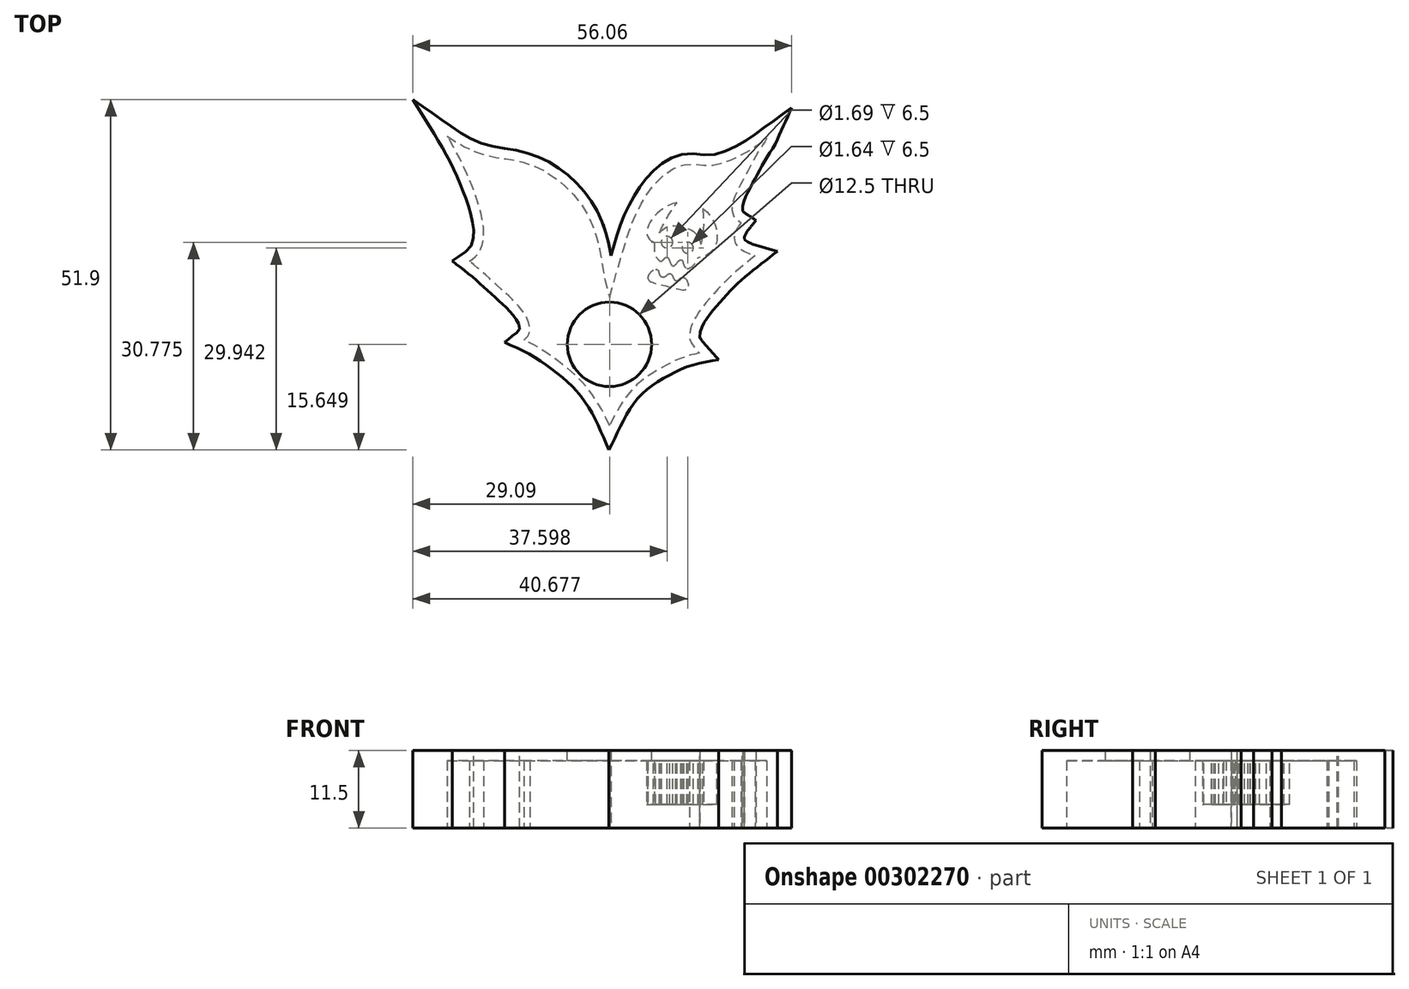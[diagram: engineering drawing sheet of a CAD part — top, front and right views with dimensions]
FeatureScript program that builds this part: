
annotation { "Feature Type Name" : "Feature", "Feature Type Description" : "" }
export const myFeature = defineFeature(function(context is Context, id is Id, definition is map)
    precondition{}
    {
        {
            var Q0;
            Q0=qCreatedBy(makeId("Top.planeOp"),FACE);
            var sketch = newSketch(context, id + "F0", { "sketchPlane" : qUnion([Q0])});
            skFitSpline(sketch, "E0", {"points": [v(0, 0) * mm, v(1.04, 3.6) * mm, v(2.03, 6.95) * mm, v(3.25, 10.76) * mm, v(4.89, 14.16) * mm, v(6.76, 16.83) * mm, v(10, 19.35) * mm, v(12.88, 19.71) * mm, v(14.8, 19.52) * mm, v(16.93, 19.96) * mm, v(18.82, 20.76) * mm, v(20.5, 21.6) * mm, v(21.92, 22.52) * mm, v(23.27, 23.54) * mm], "startDerivative": vector(11.6, 40.55) * mm, "endDerivative": vector(24.76, 17.84) * mm});
            skFitSpline(sketch, "E1", {"points": [v(23.27, 23.54) * mm, v(22.1, 21.65) * mm, v(20.11, 18.01) * mm, v(18.73, 15.37) * mm, v(18.17, 13.5) * mm, v(18.38, 12.02) * mm, v(19.5, 11.05) * mm], "startDerivative": vector(-5, -10.96) * mm, "endDerivative": vector(10.3, -6.8) * mm});
            skFitSpline(sketch, "E2", {"points": [v(19.5, 11.05) * mm, v(18.76, 9.95) * mm, v(18.55, 8.2) * mm, v(19.7, 6.95) * mm, v(21, 6.33) * mm, v(21.59, 6.15) * mm], "startDerivative": vector(-3.95, -4.92) * mm, "endDerivative": vector(3.93, -1.1) * mm});
            skFitSpline(sketch, "E3", {"points": [v(21.59, 6.15) * mm, v(17.73, 2.92) * mm, v(14.4, -0.7) * mm, v(12.34, -3.74) * mm, v(11.84, -5.76) * mm, v(13.28, -8.26) * mm], "startDerivative": vector(-16.93, -13.28) * mm, "endDerivative": vector(21.99, -24.7) * mm});
            skFitSpline(sketch, "E4", {"points": [v(13.28, -8.26) * mm, v(10.25, -9.17) * mm, v(7.27, -10.7) * mm, v(4.45, -12.6) * mm, v(1.93, -15.5) * mm, v(0, -19.05) * mm], "startDerivative": vector(-16.4, -3.11) * mm, "endDerivative": vector(-8.4, -17.05) * mm});
            skLineSegment(sketch, "E5", {"start": v(0, -19.05) * mm, "end": v(0, 0) * mm});
            skFitSpline(sketch, "E6", {"points": [v(0, -19.05) * mm, v(-0.9, -17.11) * mm, v(-2.62, -14.33) * mm, v(-4.57, -12) * mm, v(-6.78, -10.1) * mm, v(-9.56, -8.07) * mm, v(-12.7, -6.32) * mm], "startDerivative": vector(-5.74, 13.22) * mm, "endDerivative": vector(-19.61, 8.86) * mm});
            skFitSpline(sketch, "E7", {"points": [v(-12.7, -6.32) * mm, v(-12.04, -5.63) * mm, v(-11.85, -4.07) * mm, v(-13.19, -1.63) * mm, v(-15.32, 0.55) * mm, v(-17.96, 2.95) * mm, v(-20.74, 5.32) * mm], "startDerivative": vector(7, 5.62) * mm, "endDerivative": vector(-14.7, 11.22) * mm});
            skFitSpline(sketch, "E8", {"points": [v(-20.74, 5.32) * mm, v(-19.71, 6.16) * mm, v(-18.83, 7.76) * mm, v(-18.68, 10.62) * mm, v(-19.75, 14.85) * mm, v(-21.16, 18.36) * mm, v(-22.38, 20.96) * mm, v(-24.02, 23.9) * mm], "startDerivative": vector(10.92, 7.52) * mm, "endDerivative": vector(-11.35, 18.47) * mm});
            skFitSpline(sketch, "E9", {"points": [v(-24.02, 23.9) * mm, v(-21.5, 22.3) * mm, v(-18.1, 21) * mm, v(-15.1, 20.46) * mm, v(-13, 20.04) * mm, v(-9.87, 18.82) * mm, v(-6.05, 15.96) * mm, v(-3.38, 12.49) * mm, v(-1.86, 8.75) * mm, v(-1.06, 4.82) * mm, v(-0.6, 2.23) * mm, v(0, 0) * mm], "startDerivative": vector(27.7, -19.41) * mm, "endDerivative": vector(8.6, -29.29) * mm});
            skSolve(sketch);
        }
        {
            var Q0;
            Q0 = qSketchRegion(id + "F0", true);
            extrude(context, id + "F1", {"entities" : qUnion([Q0]), "depth" : 10 * mm});
        }
        {
            var Q0;
            Q0=makeQuery(id+"F1.opExtrude","CAP_FACE",FACE,{"disambiguationData":[OSD([sQuery(id+"F0.wireOp",EDGE,"E0"),sQuery(id+"F0.wireOp",EDGE,"E1"),sQuery(id+"F0.wireOp",EDGE,"E2"),sQuery(id+"F0.wireOp",EDGE,"E3"),sQuery(id+"F0.wireOp",EDGE,"E4"),sQuery(id+"F0.wireOp",EDGE,"E6"),sQuery(id+"F0.wireOp",EDGE,"E7"),sQuery(id+"F0.wireOp",EDGE,"E8"),sQuery(id+"F0.wireOp",EDGE,"E9")])],"isStart":true});
            shell(context, id + "F2", {"entities" : qUnion([Q0]), "thickness" : 1.5 * mm, "oppositeDirection" : true});
        }
        {
            var Q0;
            Q0=makeQuery(id+"F1.opExtrude","CAP_FACE",FACE,{"disambiguationData":[OSD([sQuery(id+"F0.wireOp",EDGE,"E0"),sQuery(id+"F0.wireOp",EDGE,"E1"),sQuery(id+"F0.wireOp",EDGE,"E2"),sQuery(id+"F0.wireOp",EDGE,"E3"),sQuery(id+"F0.wireOp",EDGE,"E4"),sQuery(id+"F0.wireOp",EDGE,"E6"),sQuery(id+"F0.wireOp",EDGE,"E7"),sQuery(id+"F0.wireOp",EDGE,"E8"),sQuery(id+"F0.wireOp",EDGE,"E9")])],"isStart":false});
            var sketch = newSketch(context, id + "F3", { "sketchPlane" : qUnion([Q0])});
            skCircle(sketch, "E10", {"center": v(8.5, 8.16) * mm, "radius": 0.85 * mm});
            skCircle(sketch, "E11", {"center": v(11.59, 7.32) * mm, "radius": 0.82 * mm});
            skFitSpline(sketch, "E12", {"points": [v(7.37, 9.55) * mm, v(10.45, 10.48) * mm, v(13.48, 7.8) * mm], "startDerivative": vector(6.12, 7.14) * mm, "endDerivative": vector(1.27, -11.01) * mm});
            skFitSpline(sketch, "E13", {"points": [v(7.37, 9.55) * mm, v(9.98, 13.98) * mm], "startDerivative": vector(2.21, 4.52) * mm, "endDerivative": vector(3.42, 4.33) * mm});
            skFitSpline(sketch, "E14", {"points": [v(13.78, 13.16) * mm, v(13.48, 7.8) * mm], "startDerivative": vector(0.63, -5.05) * mm, "endDerivative": vector(-1.54, -5.1) * mm});
            skFitSpline(sketch, "E15", {"points": [v(13.78, 13.16) * mm, v(15.93, 8.86) * mm, v(13.14, 5.81) * mm], "startDerivative": vector(7.9, -5.3) * mm, "endDerivative": vector(-11.8, -2.2) * mm});
            skFitSpline(sketch, "E16", {"points": [v(9.98, 13.98) * mm, v(6.63, 11.99) * mm, v(6.54, 8.19) * mm], "startDerivative": vector(-3.92, -0.2) * mm, "endDerivative": vector(10.17, -4.16) * mm});
            skFitSpline(sketch, "E17", {"points": [v(6.54, 8.19) * mm, v(7.39, 5.43) * mm], "startDerivative": vector(0.96, -1.06) * mm, "endDerivative": vector(3.78, -3.06) * mm});
            skFitSpline(sketch, "E18", {"points": [v(7.39, 5.43) * mm, v(8.54, 5.91) * mm], "startDerivative": vector(1.52, -1.24) * mm, "endDerivative": vector(1.38, -0.47) * mm});
            skFitSpline(sketch, "E19", {"points": [v(8.54, 5.91) * mm, v(9.39, 4.63) * mm], "startDerivative": vector(1, 0) * mm, "endDerivative": vector(1.28, -0.38) * mm});
            skFitSpline(sketch, "E20", {"points": [v(9.39, 4.63) * mm, v(10.6, 5.55) * mm], "startDerivative": vector(1.06, -0.31) * mm, "endDerivative": vector(1, -0.3) * mm});
            skFitSpline(sketch, "E21", {"points": [v(10.6, 5.55) * mm, v(11.46, 4.24) * mm], "startDerivative": vector(1.03, 0.13) * mm, "endDerivative": vector(1.87, -0.7) * mm});
            skFitSpline(sketch, "E22", {"points": [v(11.46, 4.24) * mm, v(13.14, 5.81) * mm], "startDerivative": vector(1.5, -0.32) * mm, "endDerivative": vector(0.8, 2.16) * mm});
            skFitSpline(sketch, "E23", {"points": [v(5.71, 2.83) * mm, v(8.45, 1.66) * mm, v(11.53, 1.28) * mm], "startDerivative": vector(-0.49, -3.62) * mm, "endDerivative": vector(2.65, 2.57) * mm});
            skFitSpline(sketch, "E24", {"points": [v(5.71, 2.83) * mm, v(6.07, 3.66) * mm, v(6.84, 4.13) * mm], "startDerivative": vector(0.2, 1.79) * mm, "endDerivative": vector(1.53, 0.02) * mm});
            skFitSpline(sketch, "E25", {"points": [v(6.84, 4.13) * mm, v(7.3, 3.74) * mm, v(7.74, 3.03) * mm], "startDerivative": vector(2.21, -0.13) * mm, "endDerivative": vector(1.85, -0.55) * mm});
            skFitSpline(sketch, "E26", {"points": [v(7.74, 3.03) * mm, v(8.43, 3.2) * mm, v(8.91, 3.52) * mm], "startDerivative": vector(1.7, -0.42) * mm, "endDerivative": vector(1.37, -0.04) * mm});
            skFitSpline(sketch, "E27", {"points": [v(8.91, 3.52) * mm, v(9.4, 3.03) * mm, v(9.8, 2.48) * mm], "startDerivative": vector(1.45, -0.02) * mm, "endDerivative": vector(1.56, -0.4) * mm});
            skFitSpline(sketch, "E28", {"points": [v(9.8, 2.48) * mm, v(10.32, 2.65) * mm, v(11.01, 2.9) * mm], "startDerivative": vector(2.07, -0.5) * mm, "endDerivative": vector(2.08, -0.31) * mm});
            skFitSpline(sketch, "E29", {"points": [v(11.01, 2.9) * mm, v(11.6, 2.1) * mm, v(11.53, 1.28) * mm], "startDerivative": vector(1.82, -0.39) * mm, "endDerivative": vector(-1.23, -1.54) * mm});
            skSolve(sketch);
        }
        {
            var Q0;
            Q0=makeQuery(id+"F3.imprint","IMPRINT",FACE,{"disambiguationData":[TD([[makeQuery(id+"F3.imprint","IMPRINT",EDGE,{"derivedFrom":sQuery(id+"F3.wireOp",EDGE,"E10")}),-1.0]])]});
            var Q1;
            Q1=makeQuery(id+"F3.imprint","IMPRINT",FACE,{"disambiguationData":[TD([[makeQuery(id+"F3.imprint","IMPRINT",EDGE,{"derivedFrom":sQuery(id+"F3.wireOp",EDGE,"E23")}),1.0]])]});
            extrude(context, id + "F4", {"entities" : qUnion([Q0, Q1]), "operationType" : NewBodyOperationType.ADD, "oppositeDirection" : true, "depth" : 8 * mm, "offsetDistance" : 25 * mm});
        }
        {
            var Q0;
            Q0=makeQuery(id+"F1.opExtrude","CAP_FACE",FACE,{"disambiguationData":[OSD([sQuery(id+"F0.wireOp",EDGE,"E0"),sQuery(id+"F0.wireOp",EDGE,"E1"),sQuery(id+"F0.wireOp",EDGE,"E2"),sQuery(id+"F0.wireOp",EDGE,"E3"),sQuery(id+"F0.wireOp",EDGE,"E4"),sQuery(id+"F0.wireOp",EDGE,"E6"),sQuery(id+"F0.wireOp",EDGE,"E7"),sQuery(id+"F0.wireOp",EDGE,"E8"),sQuery(id+"F0.wireOp",EDGE,"E9")])],"isStart":false});
            var sketch = newSketch(context, id + "F5", { "sketchPlane" : qUnion([Q0])});
            skCircle(sketch, "E30", {"center": v(0, -6.97) * mm, "radius": 6.25 * mm});
            skSolve(sketch);
        }
        {
            var Q0;
            Q0 = qSketchRegion(id + "F5", true);
            extrude(context, id + "F6", {"entities" : qUnion([Q0]), "operationType" : NewBodyOperationType.REMOVE, "oppositeDirection" : true, "depth" : 1.5 * mm});
        }
    });
